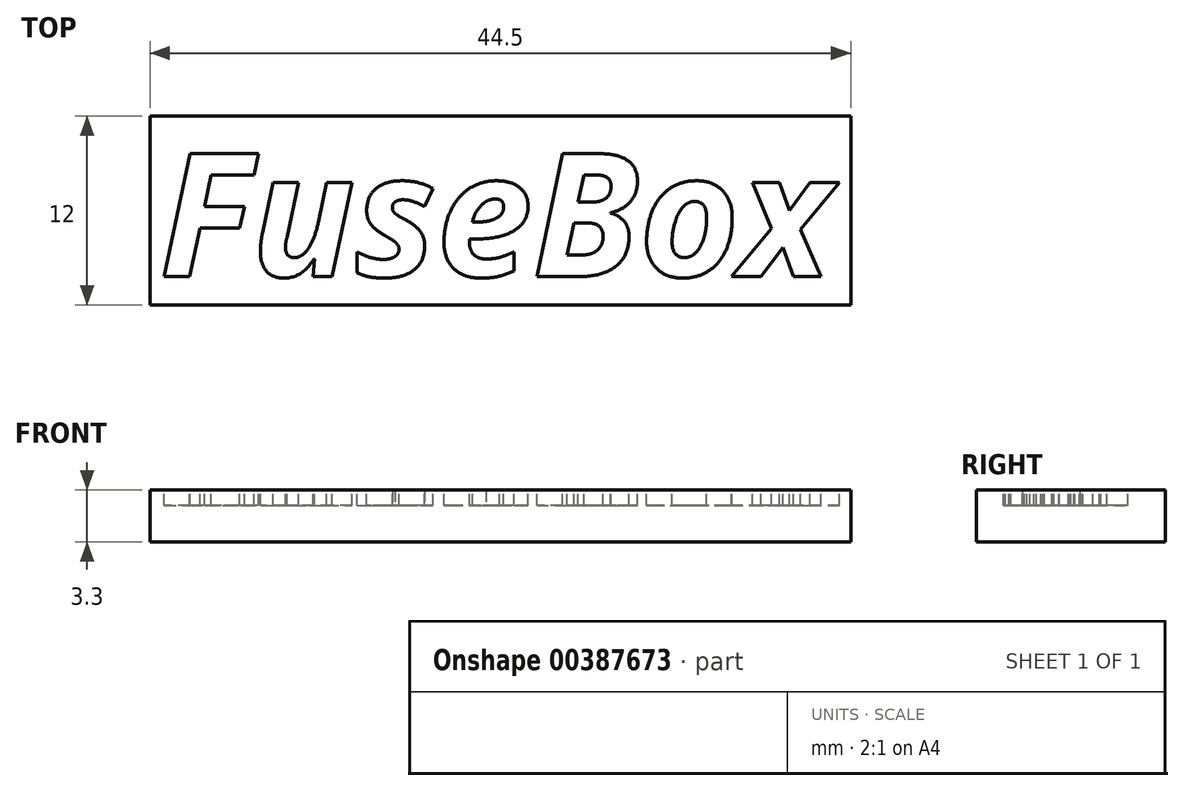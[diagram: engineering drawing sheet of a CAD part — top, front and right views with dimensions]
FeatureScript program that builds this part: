
annotation { "Feature Type Name" : "Feature", "Feature Type Description" : "" }
export const myFeature = defineFeature(function(context is Context, id is Id, definition is map)
    precondition{}
    {
        {
            var Q0;
            Q0=qCreatedBy(makeId("Top.planeOp"),FACE);
            var sketch = newSketch(context, id + "F0", { "sketchPlane" : qUnion([Q0])});
            skLineSegment(sketch, "E0.bottom", {"start": v(-10.85, 6.19) * mm, "end": v(33.65, 6.19) * mm});
            skLineSegment(sketch, "E0.top", {"start": v(-10.85, -5.81) * mm, "end": v(33.65, -5.81) * mm});
            skLineSegment(sketch, "E0.left", {"start": v(-10.85, 6.19) * mm, "end": v(-10.85, -5.81) * mm});
            skLineSegment(sketch, "E0.right", {"start": v(33.65, 6.19) * mm, "end": v(33.65, -5.81) * mm});
            skSolve(sketch);
        }
        {
            var Q0;
            Q0 = qSketchRegion(id + "F0", true);
            extrude(context, id + "F1", {"entities" : qUnion([Q0]), "depth" : 3.3 * mm});
        }
        {
            var Q0;
            Q0=makeQuery(id+"F1.opExtrude","CAP_FACE",FACE,{"disambiguationData":[OSD([sQuery(id+"F0.wireOp",EDGE,"E0.bottom"),sQuery(id+"F0.wireOp",EDGE,"E0.top"),sQuery(id+"F0.wireOp",EDGE,"E0.left"),sQuery(id+"F0.wireOp",EDGE,"E0.right")])],"isStart":false});
            var sketch = newSketch(context, id + "F2", { "sketchPlane" : qUnion([Q0])});
            skText(sketch, "E1", { "text": "FuseBox", "fontName": "OpenSans-BoldItalic.ttf"});
            const initialGuessF2  = {"E1": [-0.01024, -0.004, 1, 0, 0.00787]};
            skSetInitialGuess(sketch, initialGuessF2);
            skSolve(sketch);
        }
        {
            var Q0;
            Q0=makeQuery(id+"F2.imprint","IMPRINT",FACE,{"disambiguationData":[TD([[makeQuery(id+"F2.imprint","IMPRINT",EDGE,{"derivedFrom":sQuery(id+"F2.wireOp",EDGE,"E1.sketch_text.stroke-50")}),-1.0]])]});
            var Q1;
            Q1=makeQuery(id+"F2.imprint","IMPRINT",FACE,{"disambiguationData":[TD([[makeQuery(id+"F2.imprint","IMPRINT",EDGE,{"derivedFrom":sQuery(id+"F2.wireOp",EDGE,"E1.sketch_text.stroke-74")}),-1.0]])]});
            var Q2;
            Q2=makeQuery(id+"F2.imprint","IMPRINT",FACE,{"disambiguationData":[TD([[makeQuery(id+"F2.imprint","IMPRINT",EDGE,{"derivedFrom":sQuery(id+"F2.wireOp",EDGE,"E1.sketch_text.stroke-98")}),-1.0]])]});
            var Q3;
            Q3=makeQuery(id+"F2.imprint","IMPRINT",FACE,{"disambiguationData":[TD([[makeQuery(id+"F2.imprint","IMPRINT",EDGE,{"derivedFrom":sQuery(id+"F2.wireOp",EDGE,"E1.sketch_text.stroke-116")}),-1.0]])]});
            var Q4;
            Q4=makeQuery(id+"F2.imprint","IMPRINT",FACE,{"disambiguationData":[TD([[makeQuery(id+"F2.imprint","IMPRINT",EDGE,{"derivedFrom":sQuery(id+"F2.wireOp",EDGE,"E1.sketch_text.stroke-27")}),-1.0]])]});
            var Q5;
            Q5=makeQuery(id+"F2.imprint","IMPRINT",FACE,{"disambiguationData":[TD([[makeQuery(id+"F2.imprint","IMPRINT",EDGE,{"derivedFrom":sQuery(id+"F2.wireOp",EDGE,"E1.sketch_text.stroke-10")}),-1.0]])]});
            var Q6;
            Q6=makeQuery(id+"F2.imprint","IMPRINT",FACE,{"disambiguationData":[TD([[makeQuery(id+"F2.imprint","IMPRINT",EDGE,{"derivedFrom":sQuery(id+"F2.wireOp",EDGE,"E1.sketch_text.stroke-0")}),-1.0]])]});
            extrude(context, id + "F3", {"entities" : qUnion([Q0, Q1, Q2, Q3, Q4, Q5, Q6]), "operationType" : NewBodyOperationType.REMOVE, "oppositeDirection" : true, "depth" : 1 * mm});
        }
    });
